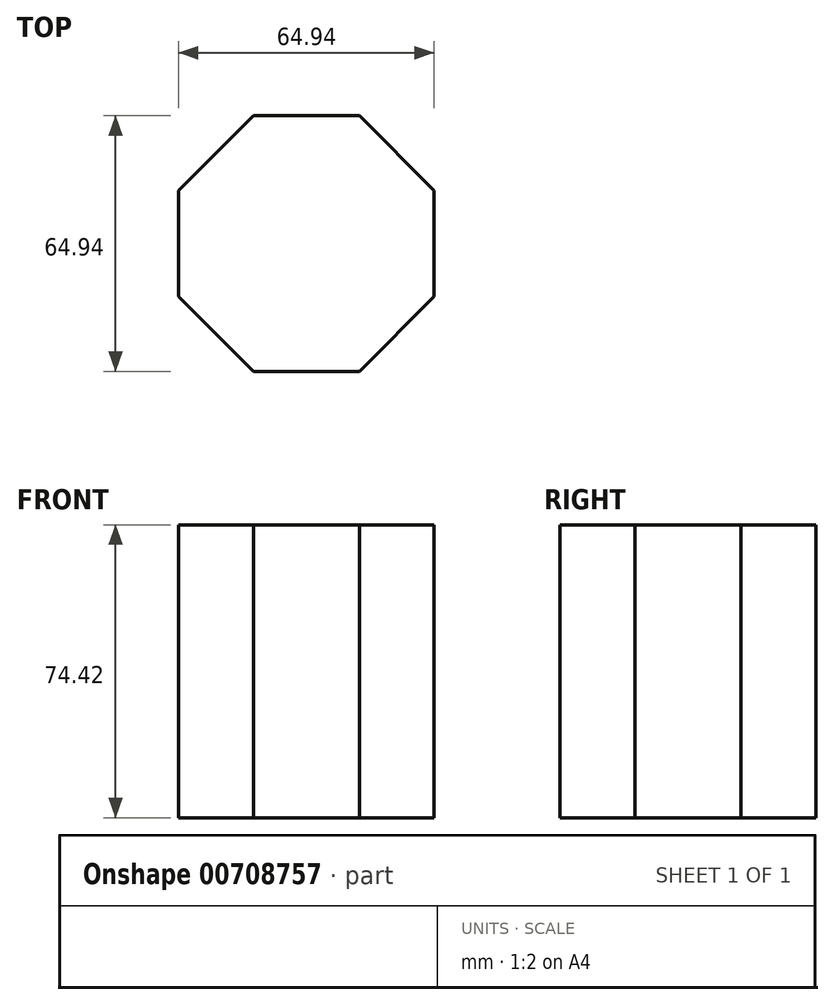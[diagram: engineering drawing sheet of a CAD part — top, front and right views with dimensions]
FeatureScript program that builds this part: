
annotation { "Feature Type Name" : "Feature", "Feature Type Description" : "" }
export const myFeature = defineFeature(function(context is Context, id is Id, definition is map)
    precondition{}
    {
        {
            var Q0;
            Q0=qCreatedBy(makeId("Top.planeOp"),FACE);
            var sketch = newSketch(context, id + "F0", { "sketchPlane" : qUnion([Q0])});
            skCircle(sketch, "E0.cCircle", {"center": v(0, 0) * mm, "radius": 32.47 * mm, "construction": true});
            skLineSegment(sketch, "E0.0", {"start": v(-32.47, 13.45) * mm, "end": v(-32.47, -13.45) * mm});
            skLineSegment(sketch, "E0.1", {"start": v(-13.45, 32.47) * mm, "end": v(-32.47, 13.45) * mm});
            skLineSegment(sketch, "E0.2", {"start": v(13.45, 32.47) * mm, "end": v(-13.45, 32.47) * mm});
            skLineSegment(sketch, "E0.3", {"start": v(32.47, 13.45) * mm, "end": v(13.45, 32.47) * mm});
            skLineSegment(sketch, "E0.4", {"start": v(32.47, -13.45) * mm, "end": v(32.47, 13.45) * mm});
            skLineSegment(sketch, "E0.5", {"start": v(13.45, -32.47) * mm, "end": v(32.47, -13.45) * mm});
            skLineSegment(sketch, "E0.6", {"start": v(-13.45, -32.47) * mm, "end": v(13.45, -32.47) * mm});
            skLineSegment(sketch, "E0.7", {"start": v(-32.47, -13.45) * mm, "end": v(-13.45, -32.47) * mm});
            skPoint(sketch, "E0.0.midPoint", {"position": v(-32.47, 0) * mm});
            skSolve(sketch);
        }
        {
            var Q0;
            Q0 = qSketchRegion(id + "F0", true);
            extrude(context, id + "F1", {"entities" : qUnion([Q0]), "depth" : 74.42 * mm, "offsetDistance" : 25.4 * mm});
        }
    });
